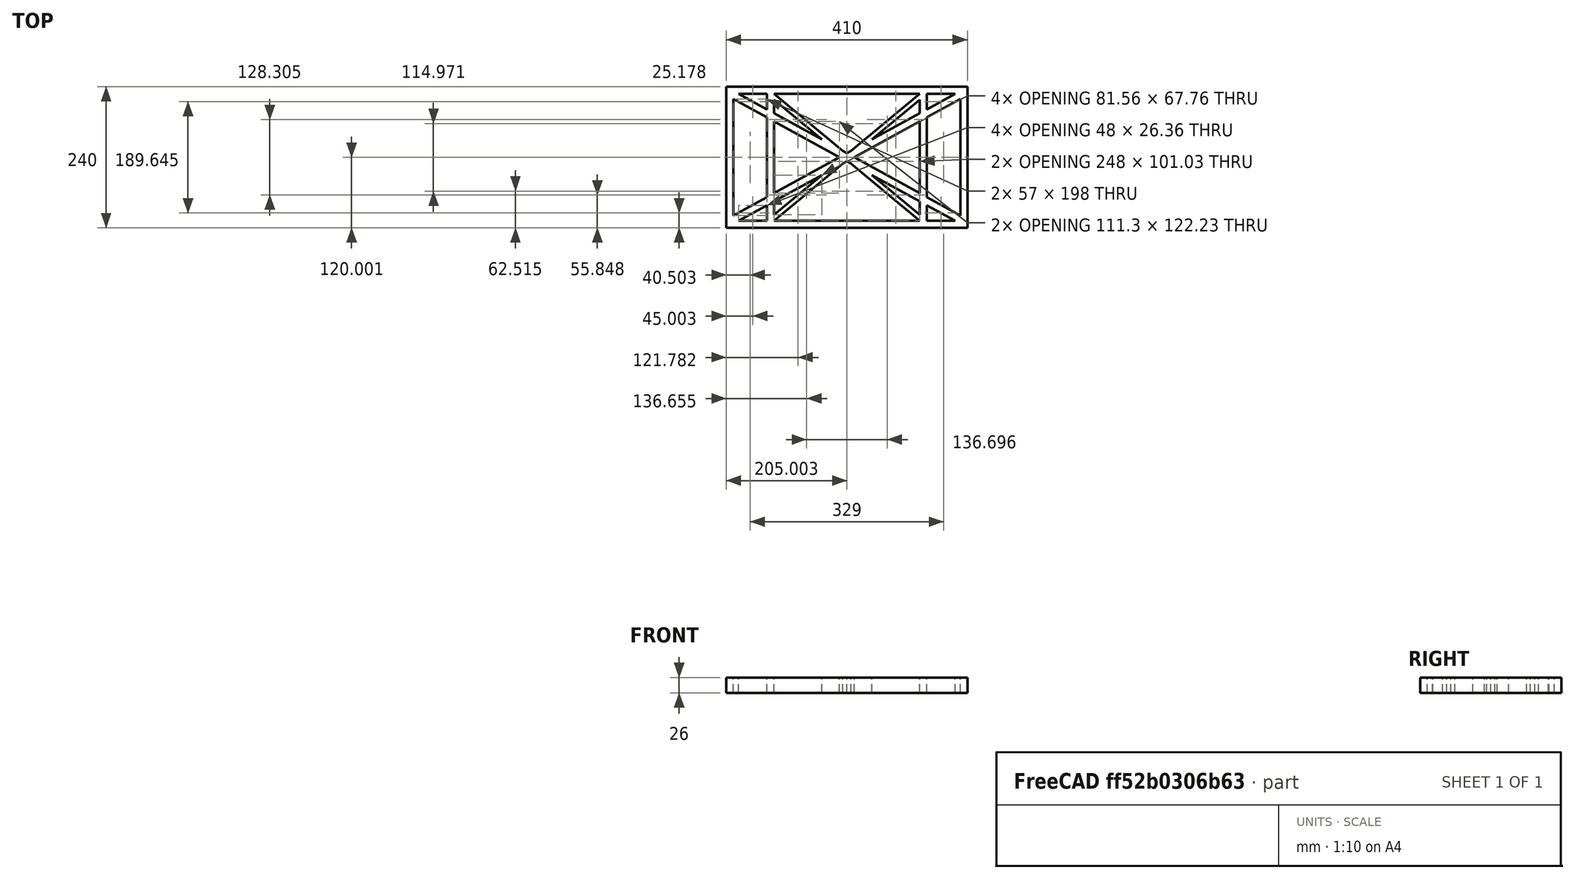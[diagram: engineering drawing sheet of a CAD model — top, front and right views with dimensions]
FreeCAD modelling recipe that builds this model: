
FCSTD DOCUMENT  (FreeCAD 0.19R0.19.2)
Label: laptopStand017
License: All rights reserved
LicenseURL: http://en.wikipedia.org/wiki/All_rights_reserved
objects: Sketcher::SketchObject×1, Part::Extrusion×1
note: 2 computed .brp shape members not serialized (recipe doc carries the construction recipe); baked Part::Feature solids carry a one-line shape summary decoded from their .brp

FEATURE [Sketcher::SketchObject] Sketch
  FullyConstrained = true
  sketch-geometry (52):
    g0: LineSegment StartX=-22.9272 StartY=136.221 StartZ=0 EndX=-22.9272 EndY=-103.779 EndZ=0
    g1: LineSegment StartX=-22.9272 StartY=136.221 StartZ=0 EndX=387.073 EndY=136.221 EndZ=0
    g2: LineSegment StartX=-22.9272 StartY=-103.779 StartZ=0 EndX=387.073 EndY=-103.779 EndZ=0
    g3: LineSegment StartX=387.073 StartY=136.221 StartZ=0 EndX=387.073 EndY=-103.779 EndZ=0
    g4: LineSegment StartX=375.073 StartY=115.221 StartZ=0 EndX=318.073 EndY=83.9235 EndZ=0
    g5: LineSegment StartX=-10.9272 StartY=-82.7794 StartZ=0 EndX=46.0728 EndY=-51.4823 EndZ=0
    g6: LineSegment StartX=-1.92719 StartY=124.221 StartZ=0 EndX=46.0728 EndY=97.8651 EndZ=0
    g7: LineSegment StartX=366.073 StartY=-91.7794 StartZ=0 EndX=318.073 EndY=-65.424 EndZ=0
    g8: LineSegment StartX=-10.9272 StartY=115.221 StartZ=0 EndX=-10.9272 EndY=-82.7794 EndZ=0
    g9: LineSegment StartX=375.073 StartY=-82.7794 StartZ=0 EndX=375.073 EndY=115.221 EndZ=0
    g10: LineSegment StartX=-1.92719 StartY=-91.7794 StartZ=0 EndX=46.0728 EndY=-91.7794 EndZ=0
    g11: LineSegment StartX=318.073 StartY=124.221 StartZ=0 EndX=366.073 EndY=124.221 EndZ=0
    g12: LineSegment StartX=306.073 StartY=-81.8102 StartZ=0 EndX=224.513 EndY=-14.0532 EndZ=0
    g13: LineSegment StartX=58.0728 StartY=114.251 StartZ=0 EndX=139.632 EndY=46.4944 EndZ=0
    g14: LineSegment StartX=306.073 StartY=124.221 StartZ=0 EndX=189.124 EndY=27.0628 EndZ=0
    g15: LineSegment StartX=58.0728 StartY=-91.7794 StartZ=0 EndX=175.022 EndY=5.37834 EndZ=0
    g16: LineSegment StartX=46.0728 StartY=124.221 StartZ=0 EndX=46.0728 EndY=97.8651 EndZ=0
    g17: LineSegment StartX=58.0728 StartY=-81.8102 StartZ=0 EndX=58.0728 EndY=-58.8351 EndZ=0
    g18: LineSegment StartX=318.073 StartY=124.221 StartZ=0 EndX=318.073 EndY=97.8651 EndZ=0
    g19: LineSegment StartX=306.073 StartY=114.251 StartZ=0 EndX=306.073 EndY=91.2763 EndZ=0
    g20: LineSegment StartX=182.073 StartY=23.1914 StartZ=0 EndX=189.124 EndY=27.0628 EndZ=0
    g21: LineSegment StartX=182.073 StartY=9.24976 StartZ=0 EndX=175.022 EndY=5.37834 EndZ=0
    g22: LineSegment StartX=224.513 StartY=46.4944 StartZ=0 EndX=306.073 EndY=114.251 EndZ=0
    g23: LineSegment StartX=175.022 StartY=27.0628 StartZ=0 EndX=58.0728 EndY=124.221 EndZ=0
    g24: LineSegment StartX=169.377 StartY=16.2206 StartZ=0 EndX=58.0728 EndY=77.3346 EndZ=0
    g25: LineSegment StartX=139.632 StartY=-14.0532 StartZ=0 EndX=58.0728 EndY=-81.8102 EndZ=0
    g26: LineSegment StartX=194.768 StartY=16.2206 StartZ=0 EndX=306.073 EndY=-44.8935 EndZ=0
    g27: LineSegment StartX=224.513 StartY=46.4944 StartZ=0 EndX=306.073 EndY=91.2763 EndZ=0
    g28: LineSegment StartX=175.022 StartY=27.0628 StartZ=0 EndX=182.073 EndY=23.1914 EndZ=0
    g29: LineSegment StartX=139.632 StartY=-14.0532 StartZ=0 EndX=58.0728 EndY=-58.8351 EndZ=0
    g30: LineSegment StartX=189.124 StartY=5.37834 StartZ=0 EndX=182.073 EndY=9.24976 EndZ=0
    g31: LineSegment StartX=189.124 StartY=5.37834 StartZ=0 EndX=306.073 EndY=-91.7794 EndZ=0
    g32: LineSegment StartX=306.073 StartY=77.3346 StartZ=0 EndX=306.073 EndY=-44.8935 EndZ=0
    g33: LineSegment StartX=318.073 StartY=83.9235 StartZ=0 EndX=318.073 EndY=-51.4823 EndZ=0
    g34: LineSegment StartX=318.073 StartY=97.8651 StartZ=0 EndX=366.073 EndY=124.221 EndZ=0
    g35: LineSegment StartX=306.073 StartY=77.3346 StartZ=0 EndX=194.768 EndY=16.2206 EndZ=0
    g36: LineSegment StartX=306.073 StartY=-58.8351 StartZ=0 EndX=224.513 EndY=-14.0532 EndZ=0
    g37: LineSegment StartX=306.073 StartY=-58.8351 StartZ=0 EndX=306.073 EndY=-81.8102 EndZ=0
    g38: LineSegment StartX=318.073 StartY=-51.4823 StartZ=0 EndX=375.073 EndY=-82.7794 EndZ=0
    g39: LineSegment StartX=318.073 StartY=-65.424 StartZ=0 EndX=318.073 EndY=-91.7794 EndZ=0
    g40: LineSegment StartX=306.073 StartY=124.221 StartZ=0 EndX=58.0728 EndY=124.221 EndZ=0
    g41: LineSegment StartX=318.073 StartY=-91.7794 StartZ=0 EndX=366.073 EndY=-91.7794 EndZ=0
    g42: LineSegment StartX=58.0728 StartY=-91.7794 StartZ=0 EndX=306.073 EndY=-91.7794 EndZ=0
    g43: LineSegment StartX=58.0728 StartY=-44.8935 StartZ=0 EndX=58.0728 EndY=77.3346 EndZ=0
    g44: LineSegment StartX=46.0728 StartY=-65.424 StartZ=0 EndX=-1.92719 EndY=-91.7794 EndZ=0
    g45: LineSegment StartX=46.0728 StartY=-65.424 StartZ=0 EndX=46.0728 EndY=-91.7794 EndZ=0
    g46: LineSegment StartX=58.0728 StartY=-44.8935 StartZ=0 EndX=169.377 EndY=16.2206 EndZ=0
    g47: LineSegment StartX=58.0728 StartY=91.2763 StartZ=0 EndX=58.0728 EndY=114.251 EndZ=0
    g48: LineSegment StartX=46.0728 StartY=83.9235 StartZ=0 EndX=46.0728 EndY=-51.4823 EndZ=0
    g49: LineSegment StartX=46.0728 StartY=124.221 StartZ=0 EndX=-1.92719 EndY=124.221 EndZ=0
    g50: LineSegment StartX=58.0728 StartY=91.2763 StartZ=0 EndX=139.632 EndY=46.4944 EndZ=0
    g51: LineSegment StartX=46.0728 StartY=83.9235 StartZ=0 EndX=-10.9272 EndY=115.221 EndZ=0
  constraints (102):
    c: Vertical(g0)
    c: Distance(g0) = 240
    c: Horizontal(g1)
    c: Distance(g1) = 410
    c: Coincident(g1,g0)
    c: Coincident(g2,g0)
    c: Horizontal(g2)
    c: Coincident(g3,g1)
    c: Vertical(g3)
    c: Coincident(g2,g3)
    c: Block(g1)
    c: Horizontal(g10)
    c: Horizontal(g11)
    c: PointOnObject(g35,g6)
    c: Coincident(g28,g20)
    c: Coincident(g30,g21)
    c: Tangent(g7,g24)
    c: PointOnObject(g24,g5)
    c: PointOnObject(g26,g4)
    c: Coincident(g20,g14)
    c: Tangent(g20,g27)
    c: Coincident(g50,g13)
    c: Coincident(g28,g23)
    c: Coincident(g22,g27)
    c: Coincident(g21,g15)
    c: Coincident(g29,g25)
    c: Tangent(g21,g29)
    c: Coincident(g36,g12)
    c: Coincident(g31,g30)
    c: Coincident(g22,g19)
    c: Tangent(g19,g32)
    c: Tangent(g18,g33)
    c: Coincident(g27,g19)
    c: Tangent(g27,g34)
    c: Coincident(g4,g33)
    c: Coincident(g35,g32)
    c: Tangent(g4,g35)
    c: Coincident(g37,g12)
    c: Tangent(g7,g36)
    c: Tangent(g32,g37)
    c: Coincident(g26,g32)
    c: Tangent(g26,g38)
    c: Coincident(g33,g38)
    c: Coincident(g39,g7)
    c: Tangent(g33,g39)
    c: Coincident(g25,g17)
    c: Tangent(g17,g43)
    c: Coincident(g29,g17)
    c: Tangent(g29,g44)
    c: Coincident(g45,g44)
    c: Tangent(g16,g45)
    c: Coincident(g5,g48)
    c: Coincident(g46,g43)
    c: Tangent(g5,g46)
    c: Tangent(g43,g47)
    c: Tangent(g16,g48)
    c: Coincident(g13,g47)
    c: PointOnObject(g40,g23)
    c: Tangent(g40,g49)
    c: Coincident(g6,g16)
    c: Coincident(g50,g47)
    c: Tangent(g6,g50)
    c: Coincident(g24,g43)
    c: Coincident(g51,g48)
    c: Tangent(g24,g51)
    c: Block(g23)
    c: Block(g14)
    c: Block(g20)
    c: Block(g40)
    c: Block(g18)
    c: Block(g34)
    c: Block(g4)
    c: Block(g38)
    c: Block(g9)
    c: Block(g36)
    c: Block(g37)
    c: Block(g7)
    c: Block(g39)
    c: Block(g22)
    c: Block(g31)
    c: Block(g42)
    c: Block(g21)
    c: Block(g15)
    c: Block(g29)
    c: Block(g25)
    c: Block(g45)
    c: Block(g44)
    c: Block(g5)
    c: Block(g8)
    c: Block(g51)
    c: Block(g6)
    c: Block(g16)
    c: Block(g13)
    c: Block(g47)
    c: Block(g35)
    c: Block(g32)
    c: Block(g24)
    c: Block(g46)
    c: Block(g49)
    c: Block(g11)
    c: Block(g41)
    c: Block(g10)
FEATURE [Part::Extrusion] Extrude
  Base = -> Sketch
  Dir = (0,0,1)
  DirMode = 2
  FaceMakerClass = Part::FaceMakerBullseye
  LengthFwd = 26
  LengthRev = 0
  Solid = true
  Symmetric = false
